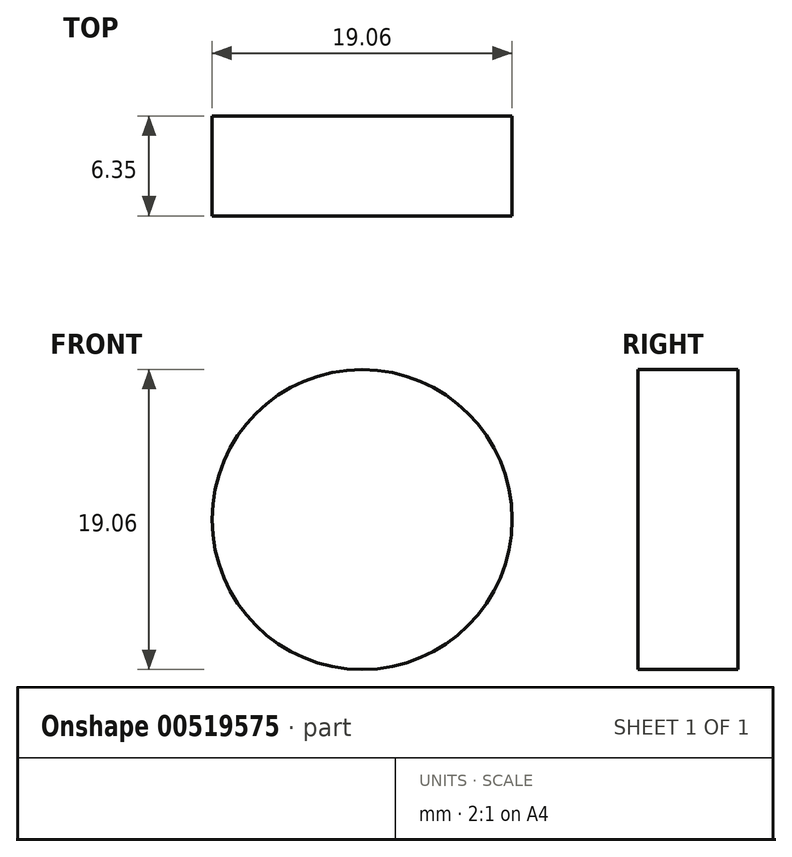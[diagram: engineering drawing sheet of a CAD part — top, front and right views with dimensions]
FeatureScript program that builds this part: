
annotation { "Feature Type Name" : "Feature", "Feature Type Description" : "" }
export const myFeature = defineFeature(function(context is Context, id is Id, definition is map)
    precondition{}
    {
        {
            var Q0;
            Q0=qCreatedBy(makeId("Front.planeOp"),FACE);
            var sketch = newSketch(context, id + "F0", { "sketchPlane" : qUnion([Q0])});
            skCircle(sketch, "E0", {"center": v(0, 0) * mm, "radius": 9.53 * mm});
            skSolve(sketch);
        }
        {
            var Q0;
            Q0 = qSketchRegion(id + "F0", true);
            extrude(context, id + "F1", {"entities" : qUnion([Q0]), "depth" : 6.35 * mm, "offsetDistance" : 25.4 * mm});
        }
    });
